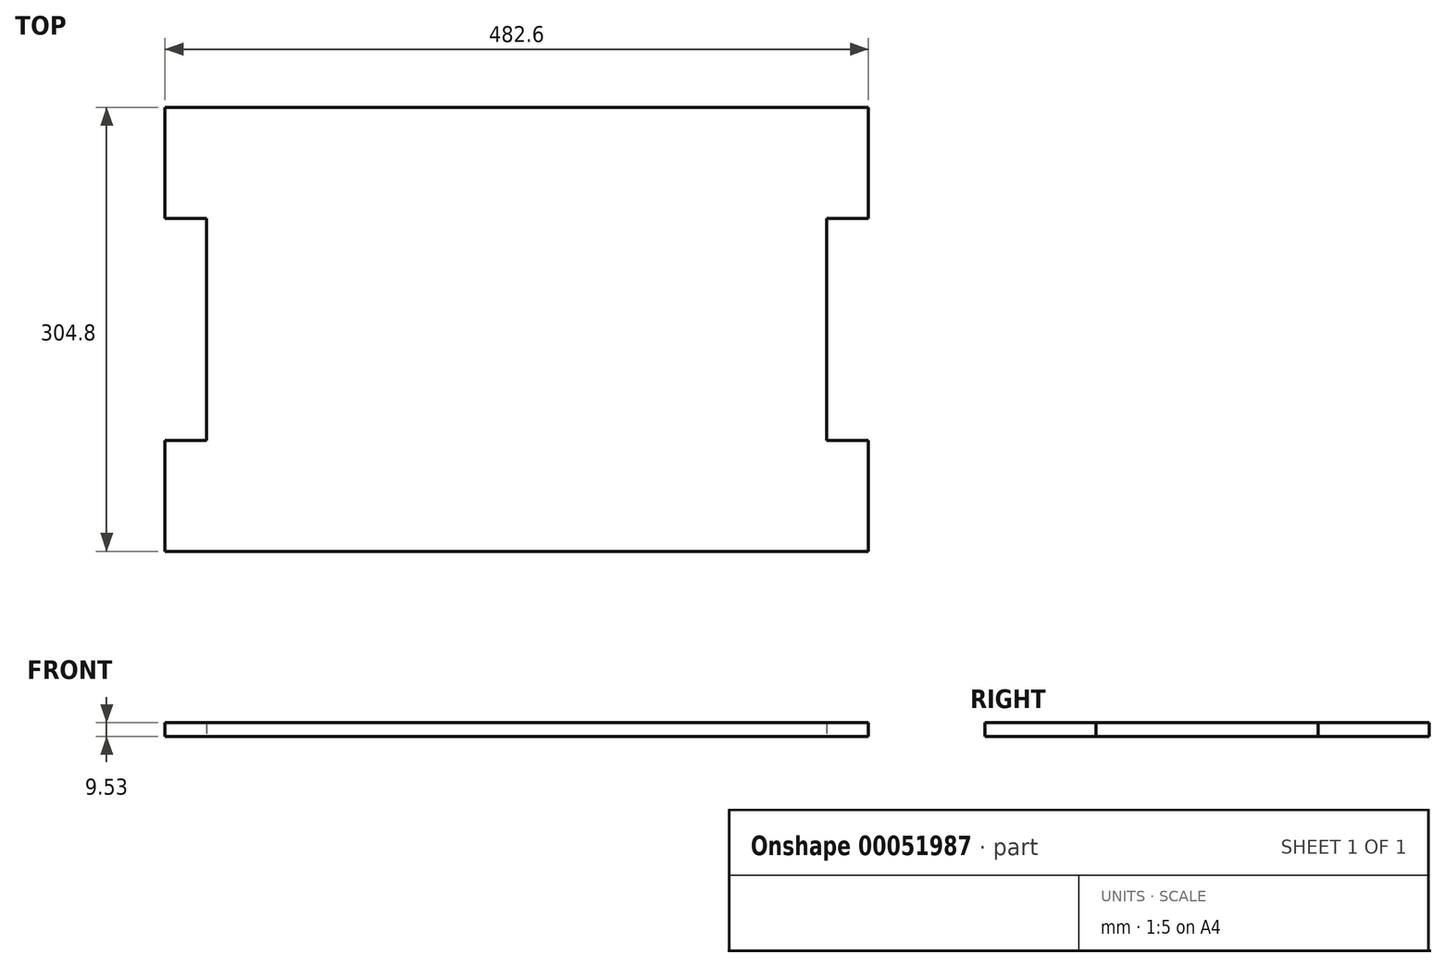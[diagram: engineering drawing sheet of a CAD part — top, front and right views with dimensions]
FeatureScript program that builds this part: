
annotation { "Feature Type Name" : "Feature", "Feature Type Description" : "" }
export const myFeature = defineFeature(function(context is Context, id is Id, definition is map)
    precondition{}
    {
        {
            var Q0;
            Q0=qCreatedBy(makeId("Top.planeOp"),FACE);
            var sketch = newSketch(context, id + "F0", { "sketchPlane" : qUnion([Q0])});
            skLineSegment(sketch, "E0.bottom", {"start": v(0, 0) * mm, "end": v(482.6, 0) * mm});
            skLineSegment(sketch, "E0.top", {"start": v(0, 304.8) * mm, "end": v(482.6, 304.8) * mm});
            skLineSegment(sketch, "E0.left", {"start": v(0, 0) * mm, "end": v(0, 304.8) * mm});
            skLineSegment(sketch, "E0.right", {"start": v(482.6, 0) * mm, "end": v(482.6, 304.8) * mm});
            skLineSegment(sketch, "E1.bottom", {"start": v(0, 228.6) * mm, "end": v(28.57, 228.6) * mm});
            skLineSegment(sketch, "E1.top", {"start": v(0, 76.2) * mm, "end": v(28.57, 76.2) * mm});
            skLineSegment(sketch, "E1.left", {"start": v(0, 228.6) * mm, "end": v(0, 76.2) * mm});
            skLineSegment(sketch, "E1.right", {"start": v(28.57, 228.6) * mm, "end": v(28.57, 76.2) * mm});
            skLineSegment(sketch, "E2.bottom", {"start": v(482.6, 228.6) * mm, "end": v(454.02, 228.6) * mm});
            skLineSegment(sketch, "E2.top", {"start": v(482.6, 76.2) * mm, "end": v(454.02, 76.2) * mm});
            skLineSegment(sketch, "E2.left", {"start": v(482.6, 228.6) * mm, "end": v(482.6, 76.2) * mm});
            skLineSegment(sketch, "E2.right", {"start": v(454.02, 228.6) * mm, "end": v(454.03, 76.2) * mm});
            skLineSegment(sketch, "E3", {"start": v(0, 152.4) * mm, "end": v(482.6, 152.4) * mm, "construction": true});
            skSolve(sketch);
        }
        {
            var Q0;
            {var subQ1=sQuery(id+"F0.wireOp",EDGE,"E0.bottom");Q0=makeQuery(id+"F0.imprint","IMPRINT",FACE,{"disambiguationData":[TD([[makeQuery(id+"F0.imprint","IMPRINT",EDGE,{"derivedFrom":subQ1}),1.0]])]});}
            extrude(context, id + "F1", {"entities" : qUnion([Q0]), "depth" : 9.52 * mm});
        }
    });
